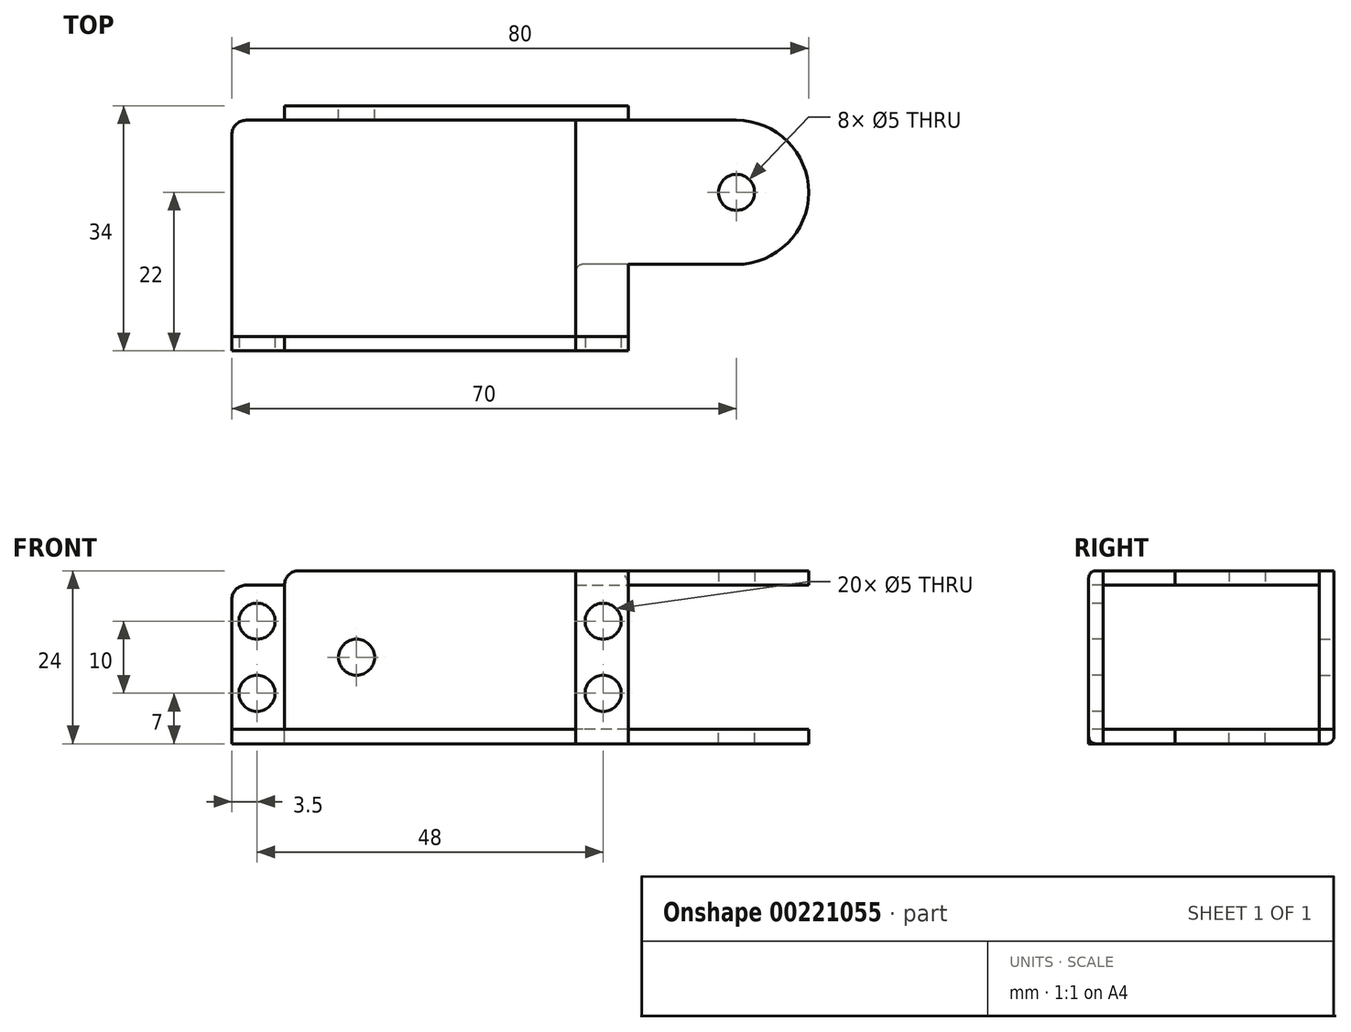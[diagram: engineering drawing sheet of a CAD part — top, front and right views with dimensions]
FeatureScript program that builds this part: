
annotation { "Feature Type Name" : "Feature", "Feature Type Description" : "" }
export const myFeature = defineFeature(function(context is Context, id is Id, definition is map)
    precondition{}
    {
        {
            var Q0;
            Q0=qCreatedBy(makeId("Front.planeOp"),FACE);
            var sketch = newSketch(context, id + "F0", { "sketchPlane" : qUnion([Q0])});
            skLineSegment(sketch, "E0.bottom", {"start": v(-27.5, 10) * mm, "end": v(-20.2, 10) * mm});
            skLineSegment(sketch, "E0.top", {"start": v(-27.5, -10) * mm, "end": v(27.5, -10) * mm});
            skLineSegment(sketch, "E0.left", {"start": v(-27.5, 10) * mm, "end": v(-27.5, -10) * mm});
            skLineSegment(sketch, "E0.right", {"start": v(27.5, 10) * mm, "end": v(27.5, -10) * mm});
            skLineSegment(sketch, "E1", {"start": v(-20.2, 10) * mm, "end": v(-20.2, -10) * mm});
            skLineSegment(sketch, "E2", {"start": v(20.2, 10) * mm, "end": v(20.2, -10) * mm});
            skCircle(sketch, "E3", {"center": v(-24, 5) * mm, "radius": 2.5 * mm});
            skCircle(sketch, "E4", {"center": v(-24, -5) * mm, "radius": 2.5 * mm});
            skCircle(sketch, "E5", {"center": v(24, 5) * mm, "radius": 2.5 * mm});
            skCircle(sketch, "E6", {"center": v(24, -5) * mm, "radius": 2.5 * mm});
            skLineSegment(sketch, "E7", {"start": v(-27.5, -10) * mm, "end": v(-27.5, -12) * mm});
            skLineSegment(sketch, "E8", {"start": v(-27.5, -12) * mm, "end": v(27.5, -12) * mm});
            skLineSegment(sketch, "E9", {"start": v(27.5, -12) * mm, "end": v(27.5, -10) * mm});
            skLineSegment(sketch, "E10", {"start": v(20.2, 10) * mm, "end": v(20.2, 12) * mm});
            skLineSegment(sketch, "E11", {"start": v(20.2, 12) * mm, "end": v(27.5, 12) * mm});
            skLineSegment(sketch, "E12", {"start": v(27.5, 12) * mm, "end": v(27.5, 10) * mm});
            skLineSegment(sketch, "E13.trimOffspring", {"start": v(20.2, 10) * mm, "end": v(27.5, 10) * mm});
            skSolve(sketch);
        }
        {
            var Q0;
            Q0=qCreatedBy(makeId("Top.planeOp"),FACE);
            var sketch = newSketch(context, id + "F1", { "sketchPlane" : qUnion([Q0])});
            skLineSegment(sketch, "E14", {"start": v(-27.5, 34) * mm, "end": v(-27.5, 2) * mm});
            skLineSegment(sketch, "E15", {"start": v(-27.5, 2) * mm, "end": v(20.2, 2) * mm});
            skLineSegment(sketch, "E16", {"start": v(-27.5, 32) * mm, "end": v(42.5, 32) * mm});
            skLineSegment(sketch, "E17", {"start": v(-27.5, 2) * mm, "end": v(-27.5, 0) * mm});
            skLineSegment(sketch, "E18", {"start": v(-27.5, 0) * mm, "end": v(27.5, 0) * mm});
            skCircle(sketch, "E19", {"center": v(42.5, 22) * mm, "radius": 2.5 * mm});
            skLineSegment(sketch, "E20", {"start": v(-27.5, 34) * mm, "end": v(27.5, 34) * mm});
            skLineSegment(sketch, "E21", {"start": v(27.5, 34) * mm, "end": v(27.5, 32) * mm});
            skLineSegment(sketch, "E22", {"start": v(42.5, 12) * mm, "end": v(42.5, 12) * mm});
            skLineSegment(sketch, "E23", {"start": v(42.5, 12) * mm, "end": v(20.2, 12) * mm});
            skLineSegment(sketch, "E24", {"start": v(20.2, 12) * mm, "end": v(20.2, 32) * mm});
            skLineSegment(sketch, "E25", {"start": v(20.2, 12) * mm, "end": v(20.2, 2) * mm});
            skLineSegment(sketch, "E26", {"start": v(20.2, 2) * mm, "end": v(20.2, 0) * mm});
            skLineSegment(sketch, "E27", {"start": v(-20.2, 2) * mm, "end": v(-20.2, 0) * mm});
            skLineSegment(sketch, "E28", {"start": v(-20.2, 32) * mm, "end": v(-20.2, 34) * mm});
            skArc(sketch, "E29", {"start": v(42.5, 12) * mm, "mid": v(52.5, 22) * mm, "end": v(42.5, 32) * mm});
            skLineSegment(sketch, "E30", {"start": v(20.2, 2) * mm, "end": v(27.5, 2) * mm});
            skLineSegment(sketch, "E31", {"start": v(27.5, 2) * mm, "end": v(27.5, 12) * mm});
            skLineSegment(sketch, "E32", {"start": v(27.5, 12) * mm, "end": v(27.5, 2) * mm});
            skLineSegment(sketch, "E33", {"start": v(27.5, 0) * mm, "end": v(27.5, 2) * mm});
            skSolve(sketch);
        }
        {
            var Q0;
            Q0=makeQuery(id+"F0.imprint","IMPRINT",FACE,{"disambiguationData":[TD([[makeQuery(id+"F0.imprint","IMPRINT",EDGE,{"derivedFrom":sQuery(id+"F0.wireOp",EDGE,"E0.bottom")}),-1.0]])]});
            var Q1;
            {var subQ0=sQuery(id+"F0.wireOp",EDGE,"E7");Q1=makeQuery(id+"F0.imprint","IMPRINT",FACE,{"disambiguationData":[TD([[makeQuery(id+"F0.imprint","IMPRINT",EDGE,{"derivedFrom":subQ0}),1.0]])]});}
            var Q2;
            {var subQ0=sQuery(id+"F0.wireOp",EDGE,"E0.right");Q2=makeQuery(id+"F0.imprint","IMPRINT",FACE,{"disambiguationData":[TD([[makeQuery(id+"F0.imprint","IMPRINT",EDGE,{"derivedFrom":subQ0}),-1.0]])]});}
            var Q3;
            Q3=makeQuery(id+"F0.imprint","IMPRINT",FACE,{"disambiguationData":[TD([[makeQuery(id+"F0.imprint","IMPRINT",EDGE,{"derivedFrom":sQuery(id+"F0.wireOp",EDGE,"E10")}),-1.0]])]});
            extrude(context, id + "F2", {"entities" : qUnion([Q0, Q1, Q2, Q3]), "oppositeDirection" : true, "depth" : 2 * mm});
        }
        {
            var Q0;
            {var subQ4=sQuery(id+"F1.wireOp",EDGE,"E15");Q0=makeQuery(id+"F1.imprint","IMPRINT",FACE,{"disambiguationData":[TD([[makeQuery(id+"F1.imprint","IMPRINT",EDGE,{"derivedFrom":subQ4}),1.0]])]});}
            var Q1;
            {var subQ8=sQuery(id+"F1.wireOp",EDGE,"E23");Q1=makeQuery(id+"F1.imprint","IMPRINT",FACE,{"disambiguationData":[TD([[makeQuery(id+"F1.imprint","IMPRINT",EDGE,{"derivedFrom":subQ8}),-1.0]])]});}
            var Q2;
            {var subQ0=sQuery(id+"F1.wireOp",EDGE,"E22");Q2=makeQuery(id+"F1.imprint","IMPRINT",FACE,{"disambiguationData":[TD([[makeQuery(id+"F1.imprint","IMPRINT",EDGE,{"derivedFrom":subQ0}),1.0]])]});}
            var Q3;
            {var subQ0=sQuery(id+"F1.wireOp",EDGE,"E21");Q3=makeQuery(id+"F1.imprint","IMPRINT",FACE,{"disambiguationData":[TD([[makeQuery(id+"F1.imprint","IMPRINT",EDGE,{"derivedFrom":subQ0}),-1.0]])]});}
            var Q4;
            {var subQ0=sQuery(id+"F1.wireOp",EDGE,"E26");Q4=makeQuery(id+"F1.imprint","IMPRINT",FACE,{"disambiguationData":[TD([[makeQuery(id+"F1.imprint","IMPRINT",EDGE,{"derivedFrom":subQ0}),-1.0]])]});}
            var Q5;
            {var subQ0=sQuery(id+"F1.wireOp",EDGE,"E17");Q5=makeQuery(id+"F1.imprint","IMPRINT",FACE,{"disambiguationData":[TD([[makeQuery(id+"F1.imprint","IMPRINT",EDGE,{"derivedFrom":subQ0}),1.0]])]});}
            extrude(context, id + "F3", {"entities" : qUnion([Q0, Q1, Q2, Q3, Q4, Q5]), "oppositeDirection" : true, "depth" : 2 * mm});
        }
        {
            var Q0;
            Q0=makeQuery(id+"F3.opExtrude","SWEPT_BODY",BODY,{"disambiguationData":[OSD([sQuery(id+"F1.wireOp",EDGE,"E14"),sQuery(id+"F1.wireOp",EDGE,"E15"),sQuery(id+"F1.wireOp",EDGE,"q6oPXj39-0zLh-izCR-QsKZ-P5NbTc8Rfou4"),sQuery(id+"F1.wireOp",EDGE,"E16"),sQuery(id+"F1.wireOp",EDGE,"E19"),sQuery(id+"F1.wireOp",EDGE,"E20"),sQuery(id+"F1.wireOp",EDGE,"E21"),sQuery(id+"F1.wireOp",EDGE,"E22")])]});
            var Q1;
            Q1=makeQuery(id+"F2.opExtrude","CAP_EDGE",EDGE,{"disambiguationData":[OSD([sQuery(id+"F0.wireOp",EDGE,"E0.left"),sQuery(id+"F0.wireOp",EDGE,"E7")])],"isStart":false});
            transform(context, id + "F4", {"entities" : qUnion([Q0]), "transformType" : TransformType.TRANSLATION_DISTANCE, "transformDirection" : qUnion([Q1]), "distance" : 10 * mm, "makeCopy" : false});
        }
        {
            var Q0;
            {var subQ8=sQuery(id+"F1.wireOp",EDGE,"E23");Q0=makeQuery(id+"F1.imprint","IMPRINT",FACE,{"disambiguationData":[TD([[makeQuery(id+"F1.imprint","IMPRINT",EDGE,{"derivedFrom":subQ8}),-1.0]])]});}
            var Q1;
            {var subQ0=sQuery(id+"F1.wireOp",EDGE,"E22");Q1=makeQuery(id+"F1.imprint","IMPRINT",FACE,{"disambiguationData":[TD([[makeQuery(id+"F1.imprint","IMPRINT",EDGE,{"derivedFrom":subQ0}),1.0]])]});}
            var Q2;
            {var subQ4=sQuery(id+"F1.wireOp",EDGE,"E23");Q2=makeQuery(id+"F1.imprint","IMPRINT",FACE,{"disambiguationData":[TD([[makeQuery(id+"F1.imprint","IMPRINT",EDGE,{"derivedFrom":subQ4}),1.0]])]});}
            extrude(context, id + "F5", {"entities" : qUnion([Q0, Q1, Q2]), "depth" : 2 * mm});
        }
        {
            var Q0;
            Q0=makeQuery(id+"F5.opExtrude","SWEPT_BODY",BODY,{"disambiguationData":[OSD([sQuery(id+"F1.wireOp",EDGE,"E15"),sQuery(id+"F1.wireOp",EDGE,"q6oPXj39-0zLh-izCR-QsKZ-P5NbTc8Rfou4"),sQuery(id+"F1.wireOp",EDGE,"E16"),sQuery(id+"F1.wireOp",EDGE,"E19"),sQuery(id+"F1.wireOp",EDGE,"E22"),sQuery(id+"F1.wireOp",EDGE,"E24"),sQuery(id+"F1.wireOp",EDGE,"E25")])]});
            var Q1;
            Q1=makeQuery(id+"F2.opExtrude","CAP_EDGE",EDGE,{"disambiguationData":[OSD([sQuery(id+"F0.wireOp",EDGE,"E0.right"),sQuery(id+"F0.wireOp",EDGE,"E9"),sQuery(id+"F0.wireOp",EDGE,"E12")])],"isStart":false});
            transform(context, id + "F6", {"entities" : qUnion([Q0]), "transformType" : TransformType.TRANSLATION_DISTANCE, "transformDirection" : qUnion([Q1]), "distance" : 10 * mm, "makeCopy" : false});
        }
        {
            var Q0;
            Q0=makeQuery(id+"F3.opExtrude","SWEPT_FACE",FACE,{"disambiguationData":[OSD([sQuery(id+"F1.wireOp",EDGE,"E20")])]});
            var sketch = newSketch(context, id + "F7", { "sketchPlane" : qUnion([Q0])});
            skLineSegment(sketch, "E34", {"start": v(-27.5, -11) * mm, "end": v(-27.5, 12) * mm});
            skLineSegment(sketch, "E35", {"start": v(-27.5, 12) * mm, "end": v(20.2, 12) * mm});
            skLineSegment(sketch, "E36", {"start": v(20.2, 12) * mm, "end": v(20.2, -12) * mm});
            skLineSegment(sketch, "E37", {"start": v(20.2, -12) * mm, "end": v(-27.5, -12) * mm});
            skLineSegment(sketch, "E38", {"start": v(-27.5, -12) * mm, "end": v(-27.5, -11) * mm});
            skLineSegment(sketch, "E39", {"start": v(-27.5, -10) * mm, "end": v(20.2, -10) * mm});
            skCircle(sketch, "E40", {"center": v(10.2, 0) * mm, "radius": 2.5 * mm});
            skSolve(sketch);
        }
        {
            var Q0;
            {var subQ2=sQuery(id+"F7.wireOp",EDGE,"E35");Q0=makeQuery(id+"F7.imprint","IMPRINT",FACE,{"disambiguationData":[TD([[makeQuery(id+"F7.imprint","IMPRINT",EDGE,{"derivedFrom":subQ2}),-1.0]])]});}
            extrude(context, id + "F8", {"entities" : qUnion([Q0]), "oppositeDirection" : true, "depth" : 2 * mm});
        }
        {
            var Q0;
            Q0=makeQuery(id+"F3.opExtrude","CAP_EDGE",EDGE,{"disambiguationData":[OSD([sQuery(id+"F1.wireOp",EDGE,"E20")])],"isStart":false});
            fillet(context, id + "F9", {"entities" : qUnion([Q0]), "radius" : 1 * mm, "tangentPropagation" : true, "allowEdgeOverflow" : false});
        }
        {
            var Q0;
            Q0=makeQuery(id+"F2.opExtrude","CAP_EDGE",EDGE,{"disambiguationData":[OSD([sQuery(id+"F0.wireOp",EDGE,"E8")])],"isStart":true});
            fillet(context, id + "F10", {"entities" : qUnion([Q0]), "radius" : 1 * mm, "tangentPropagation" : true, "allowEdgeOverflow" : false});
        }
        {
            var Q0;
            Q0=makeQuery(id+"F2.opExtrude","CAP_EDGE",EDGE,{"disambiguationData":[OSD([sQuery(id+"F0.wireOp",EDGE,"E11")])],"isStart":true});
            fillet(context, id + "F11", {"entities" : qUnion([Q0]), "radius" : 1 * mm, "tangentPropagation" : true, "allowEdgeOverflow" : false});
        }
        {
            var Q0;
            Q0=makeQuery(id+"F8.opExtrude","SWEPT_EDGE",EDGE,{"disambiguationData":[OSD([sQuery(id+"F7.wireOp",EDGE,"E34"),sQuery(id+"F7.wireOp",EDGE,"E35")])]});
            fillet(context, id + "F12", {"entities" : qUnion([Q0]), "radius" : 2 * mm, "tangentPropagation" : true, "allowEdgeOverflow" : false});
        }
        {
            var Q0;
            Q0=makeQuery(id+"F8.opExtrude","SWEPT_EDGE",EDGE,{"disambiguationData":[OSD([sQuery(id+"F7.wireOp",EDGE,"E35"),sQuery(id+"F7.wireOp",EDGE,"E36")])]});
            fillet(context, id + "F13", {"entities" : qUnion([Q0]), "radius" : 2 * mm, "tangentPropagation" : true, "allowEdgeOverflow" : false});
        }
        {
            var Q0;
            Q0=makeQuery(id+"F2.opExtrude","SWEPT_EDGE",EDGE,{"disambiguationData":[OSD([sQuery(id+"F0.wireOp",EDGE,"E0.bottom"),sQuery(id+"F0.wireOp",EDGE,"E0.left")])]});
            fillet(context, id + "F14", {"entities" : qUnion([Q0]), "radius" : 2 * mm, "tangentPropagation" : true, "allowEdgeOverflow" : false});
        }
        {
            var Q0;
            Q0=makeQuery(id+"F3.opExtrude","SWEPT_EDGE",EDGE,{"disambiguationData":[OSD([sQuery(id+"F1.wireOp",EDGE,"E14"),sQuery(id+"F1.wireOp",EDGE,"E16")])]});
            fillet(context, id + "F15", {"entities" : qUnion([Q0]), "radius" : 2 * mm, "tangentPropagation" : true, "allowEdgeOverflow" : false});
        }
        {
            var Q0;
            Q0=makeQuery(id+"F3.opExtrude","SWEPT_EDGE",EDGE,{"disambiguationData":[OSD([sQuery(id+"F1.wireOp",EDGE,"E23"),sQuery(id+"F1.wireOp",EDGE,"E24"),sQuery(id+"F1.wireOp",EDGE,"E25")])]});
            fillet(context, id + "F16", {"entities" : qUnion([Q0]), "radius" : 1 * mm, "tangentPropagation" : true, "allowEdgeOverflow" : false});
        }
    });
